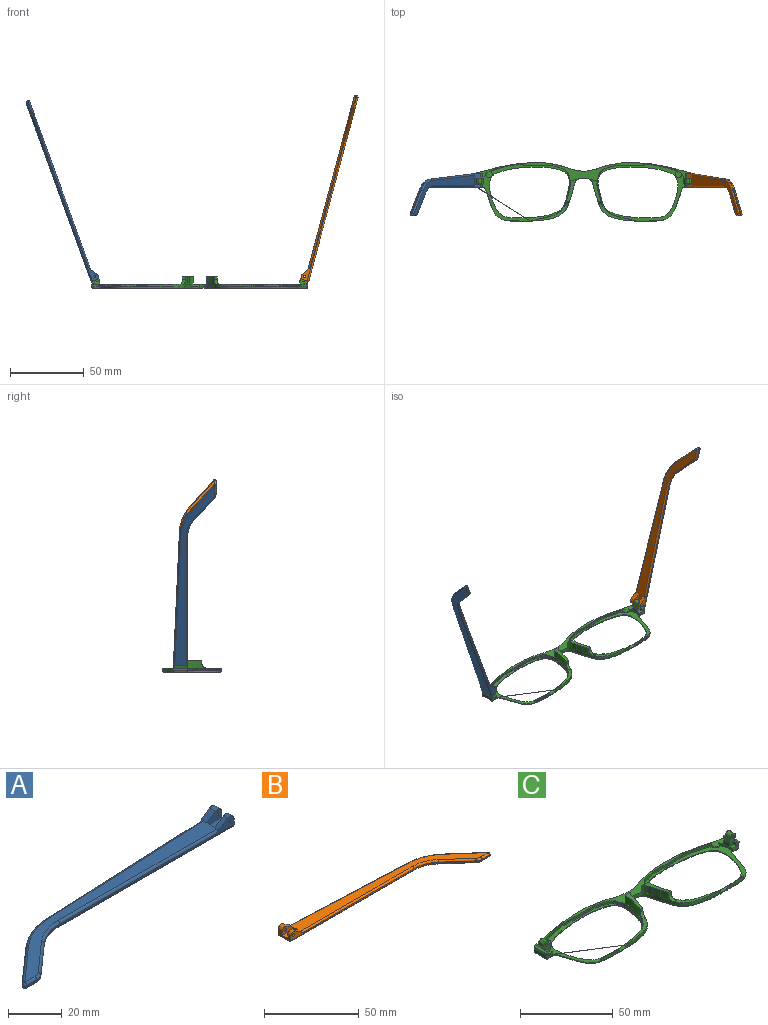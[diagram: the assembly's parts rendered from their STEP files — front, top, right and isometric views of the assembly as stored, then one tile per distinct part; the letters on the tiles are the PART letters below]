
ASSEMBLY  parts=3 mates=2
PART A: 43 faces, bbox 130.2x29.5x5.9 mm
  f0: plane 9.62x3.72mm, normal (1,0,0), area 24.7mm2, adj f1,f3,f4,f5,f10,f16,f18,f28
  f1: cylinder r=2.2mm len=3.45mm, axis (0,-1,0), area 11mm2, adj f0,f2,f4,f37
  f2: plane 6.01x3.91mm, normal (-0.55,0,0.84), area 12.7mm2, adj f1,f4,f9,f19,f37
  f3: plane 2.26x0.1mm, normal (0,0,1), area 0.1mm2, adj f0,f5,f18
  f4: plane 92.1x4.9mm, normal (0,-1,0), area 79.9mm2, adj f0,f1,f2,f14,f19,f36,f42
  f5: plane 93.42x4.13mm, normal (-0.04,1,0), area 64.8mm2, adj f0,f3,f11,f15,f17,f27,f28
  f6: plane 17.82x15.72mm, normal (-0.66,0.75,0), area 14.3mm2, adj f11,f12,f25,f30
  f7: plane 5.46x0.6mm, normal (0,-1,0), area 3.3mm2, adj f12,f13,f23,f32
  f8: plane 14.99x13.23mm, normal (0.66,-0.75,0), area 12mm2, adj f13,f14,f21,f34
  f9: plane 121.18x26.73mm, normal (0,0,1), area 627.7mm2, adj f2,f17,f19,f20,f21,f22,f23,f25
  f10: plane 129.1x27.08mm, normal (0,0,-1), area 686.5mm2, adj f0,f28,f29,f30,f32,f33,f34,f35
  f11: cylinder r=30mm len=18.52mm, axis (0,0,-1), area 12.2mm2, adj f5,f6,f26,f29
  f12: cylinder r=1mm len=1.75mm, axis (0,0,-1), area 1.5mm2, adj f6,f7,f24,f31
  f13: cylinder r=5mm len=3.31mm, axis (0,0,-1), area 2.2mm2, adj f7,f8,f22,f33
  f14: cylinder r=20mm len=13.23mm, axis (0,0,1), area 8.7mm2, adj f4,f8,f20,f35
  f15: plane 5.66x0.25mm, normal (0,0,-1), area 0.7mm2, adj f5,f17,f18
  f16: cylinder r=2.2mm len=3.45mm, axis (0,-1,0), area 14.8mm2, adj f0,f17,f18,f38
  f17: plane 6.01x3.91mm, normal (-0.55,0,0.84), area 16.9mm2, adj f5,f9,f15,f16,f18,f27,f38
  f18: plane 7.92x3.3mm, normal (0,1,0), area 15.9mm2, adj f0,f3,f15,f16,f17,f41
  f19: cylinder r=1mm len=84.18mm, axis (-1,0,0), area 131.4mm2, adj f2,f4,f9,f20
  f20: torus R=21mm, axis (0,0,1), area 23.1mm2, adj f9,f14,f19,f21
  f21: cylinder r=1mm len=15.65mm, axis (-0.75,-0.66,0), area 31.4mm2, adj f8,f9,f20,f22
  f22: torus R=4mm, axis (0,0,1), area 5.3mm2, adj f9,f13,f21,f23
  f23: cylinder r=1mm len=5.46mm, axis (-1,0,0), area 8.6mm2, adj f7,f9,f22,f24
  f24: sphere r=1mm, area 2.4mm2, adj f12,f23,f25
  f25: cylinder r=1mm len=18.48mm, axis (0.75,0.66,0), area 37.3mm2, adj f6,f9,f24,f26
  f26: torus R=29mm, axis (0,0,1), area 31.6mm2, adj f9,f11,f25,f27
  f27: cylinder r=1mm len=85.5mm, axis (1,0.04,0), area 133.5mm2, adj f5,f9,f17,f26
  f28: cylinder r=1mm len=93.46mm, axis (-1,-0.04,0), area 146.9mm2, adj f0,f5,f10,f29
  f29: torus R=29mm, axis (0,0,1), area 31.6mm2, adj f10,f11,f28,f30
  f30: cylinder r=1mm len=18.48mm, axis (-0.75,-0.66,0), area 37.3mm2, adj f6,f10,f29,f31
  f31: sphere r=1mm, area 2.4mm2, adj f12,f30,f32
  f32: cylinder r=1mm len=5.46mm, axis (1,0,0), area 8.6mm2, adj f7,f10,f31,f33
  f33: torus R=4mm, axis (0,0,1), area 5.3mm2, adj f10,f13,f32,f34
  f34: cylinder r=1mm len=15.65mm, axis (0.75,0.66,0), area 31.4mm2, adj f8,f10,f33,f35
  f35: torus R=21mm, axis (0,0,1), area 23.1mm2, adj f10,f14,f34,f36
  f36: cylinder r=1mm len=92.1mm, axis (1,0,0), area 144.7mm2, adj f0,f4,f10,f35
  f37: plane 7.92x4.7mm, normal (0,1,0), area 27mm2, adj f0,f1,f2,f39,f40,f42
  f38: plane 7.92x4.7mm, normal (0,-1,0), area 27mm2, adj f0,f16,f17,f39,f40,f41
  f39: plane 7.92x4.1mm, normal (0,0,1), area 32.5mm2, adj f0,f37,f38,f40
  f40: plane 4.1x1.4mm, normal (1,0,0), area 5.7mm2, adj f9,f37,f38,f39
  f41: cylinder r=0.5mm len=3.1mm, axis (0,-1,0), area 9.7mm2, adj f18,f38
  f42: cylinder r=0.5mm len=2.3mm, axis (0,-1,0), area 7.2mm2, adj f4,f37
PART B: 43 faces, bbox 130.2x29.5x5.9 mm
  f0: plane 9.62x3.72mm, normal (-1,0,0), area 24.7mm2, adj f1,f3,f4,f5,f10,f16,f18,f28
  f1: cylinder r=2.2mm len=3.45mm, axis (0,-1,0), area 11mm2, adj f0,f2,f4,f37
  f2: plane 6.01x3.91mm, normal (0.55,0,0.84), area 12.7mm2, adj f1,f4,f9,f19,f37
  f3: plane 2.26x0.1mm, normal (0,0,1), area 0.1mm2, adj f0,f5,f18
  f4: plane 92.1x4.9mm, normal (0,-1,0), area 78.2mm2, adj f0,f1,f2,f14,f19,f36,f42
  f5: plane 93.42x4.13mm, normal (0.04,1,0), area 64.8mm2, adj f0,f3,f11,f15,f17,f27,f28
  f6: plane 17.82x15.72mm, normal (0.66,0.75,0), area 14.3mm2, adj f11,f12,f25,f30
  f7: plane 5.46x0.6mm, normal (0,-1,0), area 3.3mm2, adj f12,f13,f23,f32
  f8: plane 14.99x13.23mm, normal (-0.66,-0.75,0), area 12mm2, adj f13,f14,f21,f34
  f9: plane 121.18x26.73mm, normal (0,0,1), area 627.7mm2, adj f2,f17,f19,f20,f21,f22,f23,f25
  f10: plane 129.1x27.08mm, normal (0,0,-1), area 686.5mm2, adj f0,f28,f29,f30,f32,f33,f34,f35
  f11: cylinder r=30mm len=18.52mm, axis (0,0,-1), area 12.2mm2, adj f5,f6,f26,f29
  f12: cylinder r=1mm len=1.75mm, axis (0,0,-1), area 1.5mm2, adj f6,f7,f24,f31
  f13: cylinder r=5mm len=3.31mm, axis (0,0,-1), area 2.2mm2, adj f7,f8,f22,f33
  f14: cylinder r=20mm len=13.23mm, axis (0,0,1), area 8.7mm2, adj f4,f8,f20,f35
  f15: plane 5.66x0.25mm, normal (0,0,-1), area 0.7mm2, adj f5,f17,f18
  f16: cylinder r=2.2mm len=3.45mm, axis (0,-1,0), area 14.8mm2, adj f0,f17,f18,f38
  f17: plane 6.01x3.91mm, normal (0.55,0,0.84), area 16.9mm2, adj f5,f9,f15,f16,f18,f27,f38
  f18: plane 7.92x3.3mm, normal (0,1,0), area 14.3mm2, adj f0,f3,f15,f16,f17,f41
  f19: cylinder r=1mm len=84.18mm, axis (1,0,0), area 131.4mm2, adj f2,f4,f9,f20
  f20: torus R=21mm, axis (0,0,1), area 23.1mm2, adj f9,f14,f19,f21
  f21: cylinder r=1mm len=15.65mm, axis (0.75,-0.66,0), area 31.4mm2, adj f8,f9,f20,f22
  f22: torus R=4mm, axis (0,0,1), area 5.3mm2, adj f9,f13,f21,f23
  f23: cylinder r=1mm len=5.46mm, axis (1,0,0), area 8.6mm2, adj f7,f9,f22,f24
  f24: sphere r=1mm, area 2.4mm2, adj f12,f23,f25
  f25: cylinder r=1mm len=18.48mm, axis (-0.75,0.66,0), area 37.3mm2, adj f6,f9,f24,f26
  f26: torus R=29mm, axis (0,0,1), area 31.6mm2, adj f9,f11,f25,f27
  f27: cylinder r=1mm len=85.5mm, axis (-1,0.04,0), area 133.5mm2, adj f5,f9,f17,f26
  f28: cylinder r=1mm len=93.46mm, axis (1,-0.04,0), area 146.9mm2, adj f0,f5,f10,f29
  f29: torus R=29mm, axis (0,0,1), area 31.6mm2, adj f10,f11,f28,f30
  f30: cylinder r=1mm len=18.48mm, axis (0.75,-0.66,0), area 37.3mm2, adj f6,f10,f29,f31
  f31: sphere r=1mm, area 2.4mm2, adj f12,f30,f32
  f32: cylinder r=1mm len=5.46mm, axis (-1,0,0), area 8.6mm2, adj f7,f10,f31,f33
  f33: torus R=4mm, axis (0,0,1), area 5.3mm2, adj f10,f13,f32,f34
  f34: cylinder r=1mm len=15.65mm, axis (-0.75,0.66,0), area 31.4mm2, adj f8,f10,f33,f35
  f35: torus R=21mm, axis (0,0,1), area 23.1mm2, adj f10,f14,f34,f36
  f36: cylinder r=1mm len=92.1mm, axis (-1,0,0), area 144.7mm2, adj f0,f4,f10,f35
  f37: plane 7.92x4.7mm, normal (0,1,0), area 25.4mm2, adj f0,f1,f2,f39,f40,f42
  f38: plane 7.92x4.7mm, normal (0,-1,0), area 25.4mm2, adj f0,f16,f17,f39,f40,f41
  f39: plane 7.92x4.1mm, normal (0,0,1), area 32.5mm2, adj f0,f37,f38,f40
  f40: plane 4.1x1.4mm, normal (-1,0,0), area 5.7mm2, adj f9,f37,f38,f39
  f41: cylinder r=0.88mm len=3.1mm, axis (0,-1,0), area 17mm2, adj f18,f38
  f42: cylinder r=0.88mm len=2.3mm, axis (0,-1,0), area 12.6mm2, adj f4,f37
PART C: 114 faces, bbox 148.1x40.9x10.4 mm
  f0: plane 3.72x1.06mm, normal (0,0,1), area 0.1mm2, adj f7,f48
  f1: plane 147.39x40.12mm, normal (0,0,1), area 449.7mm2, adj f2,f4,f7,f9,f10,f17,f29,f30
  f2: plane 1.23x0.04mm, normal (0,0,1), area 0mm2, adj f1,f9,f28
  f3: plane 2.78x2.39mm, normal (0,0,1), area 6mm2, adj f5,f9,f17,f32
  f4: plane 6.97x5.07mm, normal (0,1,0), area 22.7mm2, adj f1,f25,f26,f27,f31,f33,f34,f36
  f5: plane 3.2x2.36mm, normal (0,-1,0), area 5.7mm2, adj f3,f25,f27,f32,f35
  f6: plane 4.46x1.45mm, normal (0,0,1), area 0.1mm2, adj f7,f43
  f7: extruded ~36.19x29.29mm, area 145.5mm2, adj f0,f1,f6,f14,f17,f21,f43,f44
  f8: extruded ~13.55x2mm, area 27.2mm2, adj f13,f15,f16,f21
  f9: extruded ~38.04x16.83mm, area 106.1mm2, adj f1,f2,f3,f10,f14,f17,f19,f20
  f10: extruded ~35.39x5.69mm, area 72.2mm2, adj f1,f9,f18,f67
  f11: plane 144.78x37.85mm, normal (0,0,-1), area 477.7mm2, adj f18,f19,f21,f22,f24,f74,f75,f77
  f12: plane 59.53x38.84mm, normal (0,0,1), area 288mm2, adj f13,f14,f21,f24
  f13: extruded ~13.55x1mm, area 13.6mm2, adj f8,f12,f15
  f14: extruded ~59.02x38.34mm, area 118.1mm2, adj f7,f9,f12,f17
  f15: extruded ~13.55x1mm, area 13.6mm2, adj f8,f13,f16
  f16: plane 13.77x1.09mm, normal (0,0,1), area 3.6mm2, adj f8,f15
  f17: extruded ~59.02x38.34mm, area 114.6mm2, adj f1,f3,f7,f9,f14,f27,f50,f51
  f18: bspline ~37.01x6.7mm, area 56.6mm2, adj f10,f11,f19,f74
  f19: bspline ~45.86x8.59mm, area 59.8mm2, adj f9,f11,f18,f20
  f20: bspline ~1.04x1mm, area 0.8mm2, adj f9,f19,f22
  f21: bspline ~73.09x30.38mm, area 161.7mm2, adj f7,f8,f9,f11,f12,f23,f77
  f22: bspline ~8.61x1.2mm, area 12.6mm2, adj f9,f11,f20,f23
  f23: bspline ~1x1mm, area 0.8mm2, adj f9,f21,f22
  f24: bspline ~56.15x36.68mm, area 237.6mm2, adj f11,f12
  f25: plane 4x2.36mm, normal (-1,0,0), area 9.5mm2, adj f4,f5,f26,f27
  f26: plane 4x0.02mm, normal (0.34,0,0.94), area 0.1mm2, adj f4,f25,f34
  f27: plane 4.04x0.62mm, normal (0,0,-1), area 1.8mm2, adj f4,f5,f17,f25
  f28: plane 2.76x2.53mm, normal (0,-1,0), area 3.9mm2, adj f2,f32,f33,f41,f57
  f29: plane 7.67x1.6mm, normal (0.94,0,-0.34), area 13mm2, adj f1,f41,f42,f57
  f30: plane 2.1x1.69mm, normal (0,1,0), area 2.8mm2, adj f1,f31,f33,f42,f57
  f31: plane 3.3x2.1mm, normal (-1,0,0), area 6.9mm2, adj f1,f4,f30,f33
  f32: plane 2.35x2.1mm, normal (-1,0,0), area 4.9mm2, adj f3,f5,f28,f33,f35
  f33: plane 9.65x1.24mm, normal (0,0,1), area 8.2mm2, adj f4,f28,f30,f31,f32,f35,f36,f57
  f34: plane 4x3.31mm, normal (-0.94,0,0.34), area 14.1mm2, adj f4,f26,f35,f38
  f35: plane 5.77x5.06mm, normal (0,-1,0), area 17mm2, adj f5,f32,f33,f34,f36,f37,f38,f39
  f36: plane 4x2.21mm, normal (0.94,0,-0.34), area 9.4mm2, adj f4,f33,f35,f39
  f37: plane 4x0.01mm, normal (0.34,0,0.94), area 0mm2, adj f4,f35,f38,f39
  f38: cylinder r=1.98mm len=4mm, axis (0,1,0), area 12.4mm2, adj f4,f34,f35,f37
  f39: cylinder r=1.98mm len=4mm, axis (0,-1,0), area 12.4mm2, adj f4,f35,f36,f37
  f40: cylinder r=0.88mm len=4mm, axis (0,-1,0), area 22mm2, adj f4,f35
  f41: cone r=1mm half-angle=20deg, axis (0,0,1), area 2.3mm2, adj f1,f28,f29,f57
  f42: cylinder r=1mm len=2.28mm, axis (-0.34,0,-0.94), area 3mm2, adj f1,f29,f30,f57
  f43: extruded ~5x4.44mm, area 23.3mm2, adj f6,f7,f49
  f44: plane 2.1x2mm, normal (0,-1,0), area 4.2mm2, adj f7,f45,f49,f56
  f45: extruded ~17.45x5mm, area 78.9mm2, adj f1,f44,f46,f49,f56
  f46: plane 5x4.38mm, normal (0.14,0.99,0), area 22.1mm2, adj f1,f45,f47,f49
  f47: extruded ~5x0.06mm, area 0.4mm2, adj f1,f7,f46,f49
  f48: extruded ~5x3.64mm, area 18.9mm2, adj f0,f7,f49
  f49: plane 15.19x7.44mm, normal (0,0,1), area 35.5mm2, adj f7,f43,f44,f45,f46,f47,f48
  f50: plane 2.56x1.05mm, normal (0,0,-1), area 1mm2, adj f17,f51
  f51: cylinder r=2.28mm len=2.53mm, axis (0,0,1), area 1.4mm2, adj f1,f17,f50
  f52: plane 4.55x4.45mm, normal (0,0,-1), area 14.7mm2, adj f17,f53
  f53: cylinder r=2.28mm len=4.55mm, axis (0,0,1), area 5.2mm2, adj f1,f17,f52
  f54: plane 1.71x1.45mm, normal (0,0,-1), area 1mm2, adj f17,f55
  f55: cylinder r=1.3mm len=1.7mm, axis (0,0,1), area 1.3mm2, adj f1,f17,f54
  f56: cylinder r=3mm len=3.05mm, axis (1,0,0), area 9.5mm2, adj f1,f7,f44,f45
  f57: plane 9.71x1.44mm, normal (0.34,0,0.94), area 13.9mm2, adj f28,f29,f30,f33,f41,f42
  f58: plane 3.72x1.06mm, normal (0,0,1), area 0.1mm2, adj f64,f104
  f59: plane 1.23x0.04mm, normal (0,0,1), area 0mm2, adj f1,f66,f84
  f60: plane 2.78x2.39mm, normal (0,0,1), area 6mm2, adj f62,f66,f73,f88
  f61: plane 6.97x5.07mm, normal (0,1,0), area 22.7mm2, adj f1,f81,f82,f83,f87,f89,f90,f92
  f62: plane 3.2x2.36mm, normal (0,-1,0), area 5.7mm2, adj f60,f81,f83,f88,f91
  f63: plane 4.46x1.45mm, normal (0,0,1), area 0.1mm2, adj f64,f99
  f64: extruded ~36.19x29.29mm, area 145.5mm2, adj f1,f7,f58,f63,f70,f73,f77,f99
  f65: extruded ~13.55x2mm, area 27.2mm2, adj f69,f71,f72,f77
  f66: extruded ~38.04x16.83mm, area 106.1mm2, adj f1,f59,f60,f67,f70,f73,f75,f76
  f67: extruded ~35.39x5.69mm, area 72.2mm2, adj f1,f10,f66,f74
  f68: plane 59.53x38.84mm, normal (0,0,1), area 288mm2, adj f69,f70,f77,f80
  f69: extruded ~13.55x1mm, area 13.6mm2, adj f65,f68,f71
  f70: extruded ~59.02x38.34mm, area 118.1mm2, adj f64,f66,f68,f73
  f71: extruded ~13.55x1mm, area 13.6mm2, adj f65,f69,f72
  f72: plane 13.77x1.09mm, normal (0,0,1), area 3.6mm2, adj f65,f71
  f73: extruded ~59.02x38.34mm, area 114.6mm2, adj f1,f60,f64,f66,f70,f83,f106,f107
  f74: bspline ~37.01x6.7mm, area 56.6mm2, adj f11,f18,f67,f75
  f75: bspline ~45.86x8.59mm, area 59.8mm2, adj f11,f66,f74,f76
  f76: bspline ~1.04x1mm, area 0.7mm2, adj f66,f75,f78
  f77: bspline ~73.09x30.38mm, area 161.7mm2, adj f11,f21,f64,f65,f66,f68,f79
  f78: bspline ~8.61x1.2mm, area 12.6mm2, adj f11,f66,f76,f79
  f79: bspline ~1x1mm, area 0.8mm2, adj f66,f77,f78
  f80: bspline ~56.15x36.68mm, area 237.6mm2, adj f11,f68
  f81: plane 4x2.36mm, normal (1,0,0), area 9.5mm2, adj f61,f62,f82,f83
  f82: plane 4x0.02mm, normal (-0.34,0,0.94), area 0.1mm2, adj f61,f81,f90
  f83: plane 4.04x0.62mm, normal (0,0,-1), area 1.8mm2, adj f61,f62,f73,f81
  f84: plane 2.76x2.53mm, normal (0,-1,0), area 3.9mm2, adj f59,f88,f89,f97,f113
  f85: plane 7.67x1.6mm, normal (-0.94,0,-0.34), area 13mm2, adj f1,f97,f98,f113
  f86: plane 2.1x1.69mm, normal (0,1,0), area 2.8mm2, adj f1,f87,f89,f98,f113
  f87: plane 3.3x2.1mm, normal (1,0,0), area 6.9mm2, adj f1,f61,f86,f89
  f88: plane 2.35x2.1mm, normal (1,0,0), area 4.9mm2, adj f60,f62,f84,f89,f91
  f89: plane 9.65x1.24mm, normal (0,0,1), area 8.2mm2, adj f61,f84,f86,f87,f88,f91,f92,f113
  f90: plane 4x3.31mm, normal (0.94,0,0.34), area 14.1mm2, adj f61,f82,f91,f94
  f91: plane 5.77x5.06mm, normal (0,-1,0), area 17mm2, adj f62,f88,f89,f90,f92,f93,f94,f95
  f92: plane 4x2.21mm, normal (-0.94,0,-0.34), area 9.4mm2, adj f61,f89,f91,f95
  f93: plane 4x0.01mm, normal (-0.34,0,0.94), area 0mm2, adj f61,f91,f94,f95
  f94: cylinder r=1.98mm len=4mm, axis (0,1,0), area 12.4mm2, adj f61,f90,f91,f93
  f95: cylinder r=1.98mm len=4mm, axis (0,-1,0), area 12.4mm2, adj f61,f91,f92,f93
  f96: cylinder r=0.88mm len=4mm, axis (0,-1,0), area 22mm2, adj f61,f91
  f97: cone r=1mm half-angle=20deg, axis (0,0,1), area 2.3mm2, adj f1,f84,f85,f113
  f98: cylinder r=1mm len=2.28mm, axis (0.34,0,-0.94), area 3mm2, adj f1,f85,f86,f113
  f99: extruded ~5x4.44mm, area 23.3mm2, adj f63,f64,f105
  f100: plane 2.1x2mm, normal (0,-1,0), area 4.2mm2, adj f64,f101,f105,f112
  f101: extruded ~17.45x5mm, area 78.9mm2, adj f1,f100,f102,f105,f112
  f102: plane 5x4.38mm, normal (-0.14,0.99,0), area 22.1mm2, adj f1,f101,f103,f105
  f103: extruded ~5x0.06mm, area 0.4mm2, adj f1,f64,f102,f105
  f104: extruded ~5x3.64mm, area 18.9mm2, adj f58,f64,f105
  f105: plane 15.19x7.44mm, normal (0,0,1), area 35.5mm2, adj f64,f99,f100,f101,f102,f103,f104
  f106: plane 2.56x1.05mm, normal (0,0,-1), area 1mm2, adj f73,f107
  f107: cylinder r=2.28mm len=2.53mm, axis (0,0,1), area 1.4mm2, adj f1,f73,f106
  f108: plane 4.55x4.45mm, normal (0,0,-1), area 14.7mm2, adj f73,f109
  f109: cylinder r=2.28mm len=4.55mm, axis (0,0,1), area 5.2mm2, adj f1,f73,f108
  f110: plane 1.71x1.45mm, normal (0,0,-1), area 1mm2, adj f73,f111
  f111: cylinder r=1.3mm len=1.7mm, axis (0,0,1), area 1.3mm2, adj f1,f73,f110
  f112: cylinder r=3mm len=3.05mm, axis (-1,0,0), area 9.5mm2, adj f1,f64,f100,f101
  f113: plane 9.71x1.44mm, normal (-0.34,0,0.94), area 13.9mm2, adj f84,f85,f86,f89,f97,f98
PLACE A rot(axis=(0,1,0),70deg) t=(-84.77,-5.75,56)mm
PLACE B rot(axis=(0,-1,0),75deg) t=(68.2,-5.75,-61.61)mm
PLACE C t=(10.15,-1.13,-5.77)mm
MATE revolute A.f1 <-> C.f94  axis (0,-1,0) through (-60.89,2.72,1.22)mm
MATE revolute B.f41 <-> C.f39  axis (0,-1,0) through (81.2,2.72,1.21)mm
